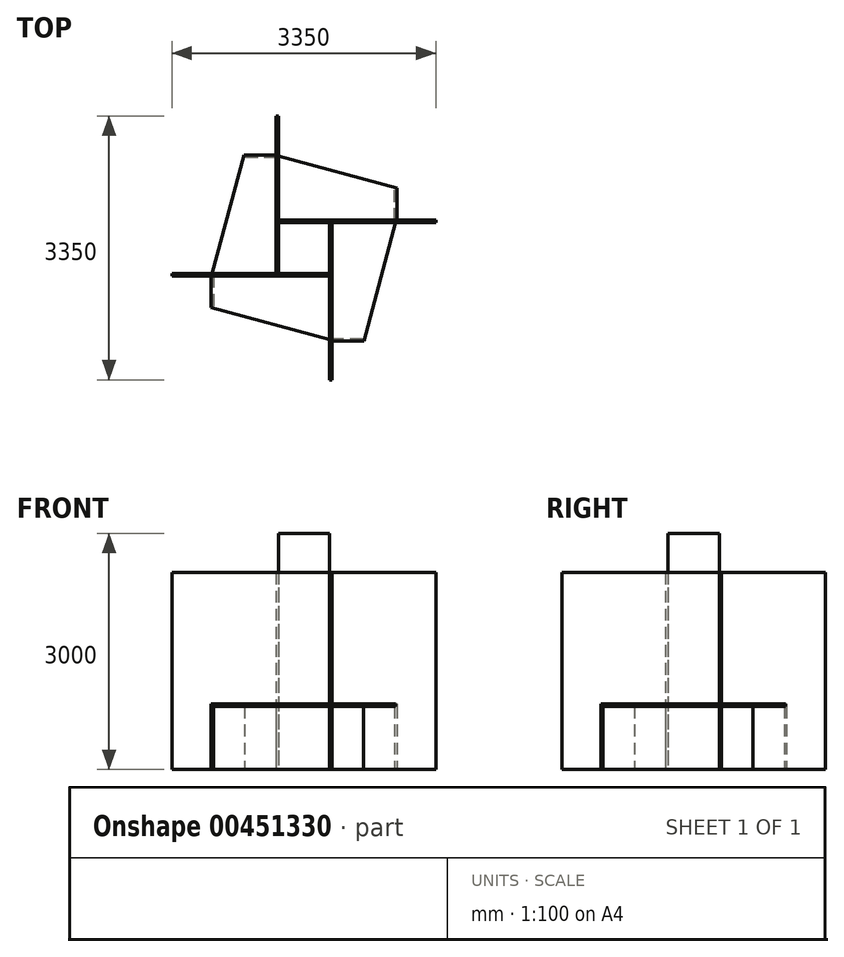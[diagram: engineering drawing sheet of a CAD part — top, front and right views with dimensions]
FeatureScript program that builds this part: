
annotation { "Feature Type Name" : "Feature", "Feature Type Description" : "" }
export const myFeature = defineFeature(function(context is Context, id is Id, definition is map)
    precondition{}
    {
        {
            var Q0;
            Q0=qCreatedBy(makeId("Top.planeOp"),FACE);
            var sketch = newSketch(context, id + "F0", { "sketchPlane" : qUnion([Q0])});
            skLineSegment(sketch, "E0.bottom", {"start": v(325, -325) * mm, "end": v(-325, -325) * mm});
            skLineSegment(sketch, "E0.top", {"start": v(325, 325) * mm, "end": v(-325, 325) * mm});
            skLineSegment(sketch, "E0.left", {"start": v(325, -325) * mm, "end": v(325, 325) * mm});
            skLineSegment(sketch, "E0.right", {"start": v(-325, -325) * mm, "end": v(-325, 325) * mm});
            skPoint(sketch, "E0.middle", {"position": v(0, 0) * mm});
            skSolve(sketch);
        }
        {
            var Q0;
            Q0 = qSketchRegion(id + "F0", true);
            extrude(context, id + "F1", {"entities" : qUnion([Q0]), "depth" : 3000 * mm});
        }
        {
            var Q0;
            Q0=qCreatedBy(makeId("Top.planeOp"),FACE);
            var sketch = newSketch(context, id + "F2", { "sketchPlane" : qUnion([Q0])});
            skLineSegment(sketch, "E1.bottom", {"start": v(325, -325) * mm, "end": v(-1675, -325) * mm});
            skLineSegment(sketch, "E1.top", {"start": v(325, -355) * mm, "end": v(-1675, -355) * mm});
            skLineSegment(sketch, "E1.left", {"start": v(325, -325) * mm, "end": v(325, -355) * mm});
            skLineSegment(sketch, "E1.right", {"start": v(-1675, -325) * mm, "end": v(-1675, -355) * mm});
            skSolve(sketch);
        }
        {
            var Q0;
            Q0 = qSketchRegion(id + "F2", true);
            extrude(context, id + "F3", {"entities" : qUnion([Q0]), "depth" : 2500 * mm});
        }
        {
            var Q0;
            Q0=qCreatedBy(makeId("Right.planeOp"),FACE);
            var sketch = newSketch(context, id + "F4", { "sketchPlane" : qUnion([Q0])});
            skLineSegment(sketch, "E2", {"start": v(0, 0) * mm, "end": v(0, 3515.64) * mm});
            skSolve(sketch);
        }
        {
            var Q0;
            Q0=makeQuery(id+"F3.opExtrude","SWEPT_BODY",BODY,{"disambiguationData":[OSD([sQuery(id+"F2.wireOp",EDGE,"E1.bottom"),sQuery(id+"F2.wireOp",EDGE,"E1.top"),sQuery(id+"F2.wireOp",EDGE,"E1.left"),sQuery(id+"F2.wireOp",EDGE,"E1.right")])]});
            var Q1;
            Q1=sQuery(id+"F4.wireOp",EDGE,"E2");
            circularPattern(context, id + "F5", {"entities" : qUnion([Q0]), "axis" : qUnion([Q1]), "angle" : 360 * degree, "instanceCount" : 4, "equalSpace" : true});
        }
        {
            var Q0;
            Q0=qCreatedBy(makeId("Top.planeOp"),FACE);
            cPlane(context, id + "F6", {"entities" : qUnion([Q0]), "cplaneType" : CPlaneType.OFFSET, "offset" : 800 * mm, "width" : 150 * mm, "height" : 150 * mm});
        }
        {
            var Q0;
            Q0=qCreatedBy(id+"F6.planeOp",FACE);
            var sketch = newSketch(context, id + "F7", { "sketchPlane" : qUnion([Q0])});
            skLineSegment(sketch, "E3", {"start": v(325, -355) * mm, "end": v(325, -1165) * mm});
            skLineSegment(sketch, "E4", {"start": v(325, -1165) * mm, "end": v(-1180, -760) * mm});
            skLineSegment(sketch, "E5", {"start": v(-1180, -760) * mm, "end": v(-1180, -355) * mm});
            skLineSegment(sketch, "E6", {"start": v(-1180, -355) * mm, "end": v(325, -355) * mm});
            skSolve(sketch);
        }
        {
            var Q0;
            Q0 = qSketchRegion(id + "F7", true);
            extrude(context, id + "F8", {"entities" : qUnion([Q0]), "depth" : 30 * mm});
        }
        {
            var Q0;
            Q0=qCreatedBy(makeId("Top.planeOp"),FACE);
            var sketch = newSketch(context, id + "F9", { "sketchPlane" : qUnion([Q0])});
            skLineSegment(sketch, "E7.bottom", {"start": v(-1180, -355) * mm, "end": v(-1150, -355) * mm});
            skLineSegment(sketch, "E7.top", {"start": v(-1180, -755) * mm, "end": v(-1150, -755) * mm});
            skLineSegment(sketch, "E7.left", {"start": v(-1180, -355) * mm, "end": v(-1180, -755) * mm});
            skLineSegment(sketch, "E7.right", {"start": v(-1150, -355) * mm, "end": v(-1150, -755) * mm});
            skSolve(sketch);
        }
        {
            var Q0;
            Q0 = qSketchRegion(id + "F9", true);
            var Q1;
            Q1=makeQuery(id+"F3.opExtrude","CAP_VERTEX",VERTEX,{"disambiguationData":[OSD([sQuery(id+"F2.wireOp",EDGE,"E1.top"),sQuery(id+"F2.wireOp",EDGE,"E1.right")])],"isStart":false});
            extrude(context, id + "F10", {"entities" : qUnion([Q0]), "endBound" : BoundingType.UP_TO_NEXT, "endBoundEntityVertex" : qUnion([Q1]), "depth" : 25 * mm});
        }
        {
            var Q0;
            Q0=makeQuery(id+"F10.opExtrude","SWEPT_BODY",BODY,{"disambiguationData":[OSD([sQuery(id+"F9.wireOp",EDGE,"E7.bottom"),sQuery(id+"F9.wireOp",EDGE,"E7.top"),sQuery(id+"F9.wireOp",EDGE,"E7.left"),sQuery(id+"F9.wireOp",EDGE,"E7.right")])]});
            var Q1;
            Q1=makeQuery(id+"FTCvSypASrffNM0_4.opPattern","COPY",BODY,{"derivedFrom":makeQuery(id+"F8.opExtrude","SWEPT_BODY",BODY,{"disambiguationData":[OSD([sQuery(id+"F7.wireOp",EDGE,"E3"),sQuery(id+"F7.wireOp",EDGE,"E4"),sQuery(id+"F7.wireOp",EDGE,"E5"),sQuery(id+"F7.wireOp",EDGE,"E6")])]}),"instanceName":"1"});
            var Q2;
            Q2=makeQuery(id+"F8.opExtrude","SWEPT_BODY",BODY,{"disambiguationData":[OSD([sQuery(id+"F7.wireOp",EDGE,"E3"),sQuery(id+"F7.wireOp",EDGE,"E4"),sQuery(id+"F7.wireOp",EDGE,"E5"),sQuery(id+"F7.wireOp",EDGE,"E6")])]});
            var Q3;
            Q3=sQuery(id+"F4.wireOp",EDGE,"E2");
            circularPattern(context, id + "F11", {"entities" : qUnion([Q0, Q1, Q2]), "axis" : qUnion([Q3]), "angle" : 360 * degree, "instanceCount" : 4, "equalSpace" : true});
        }
    });
